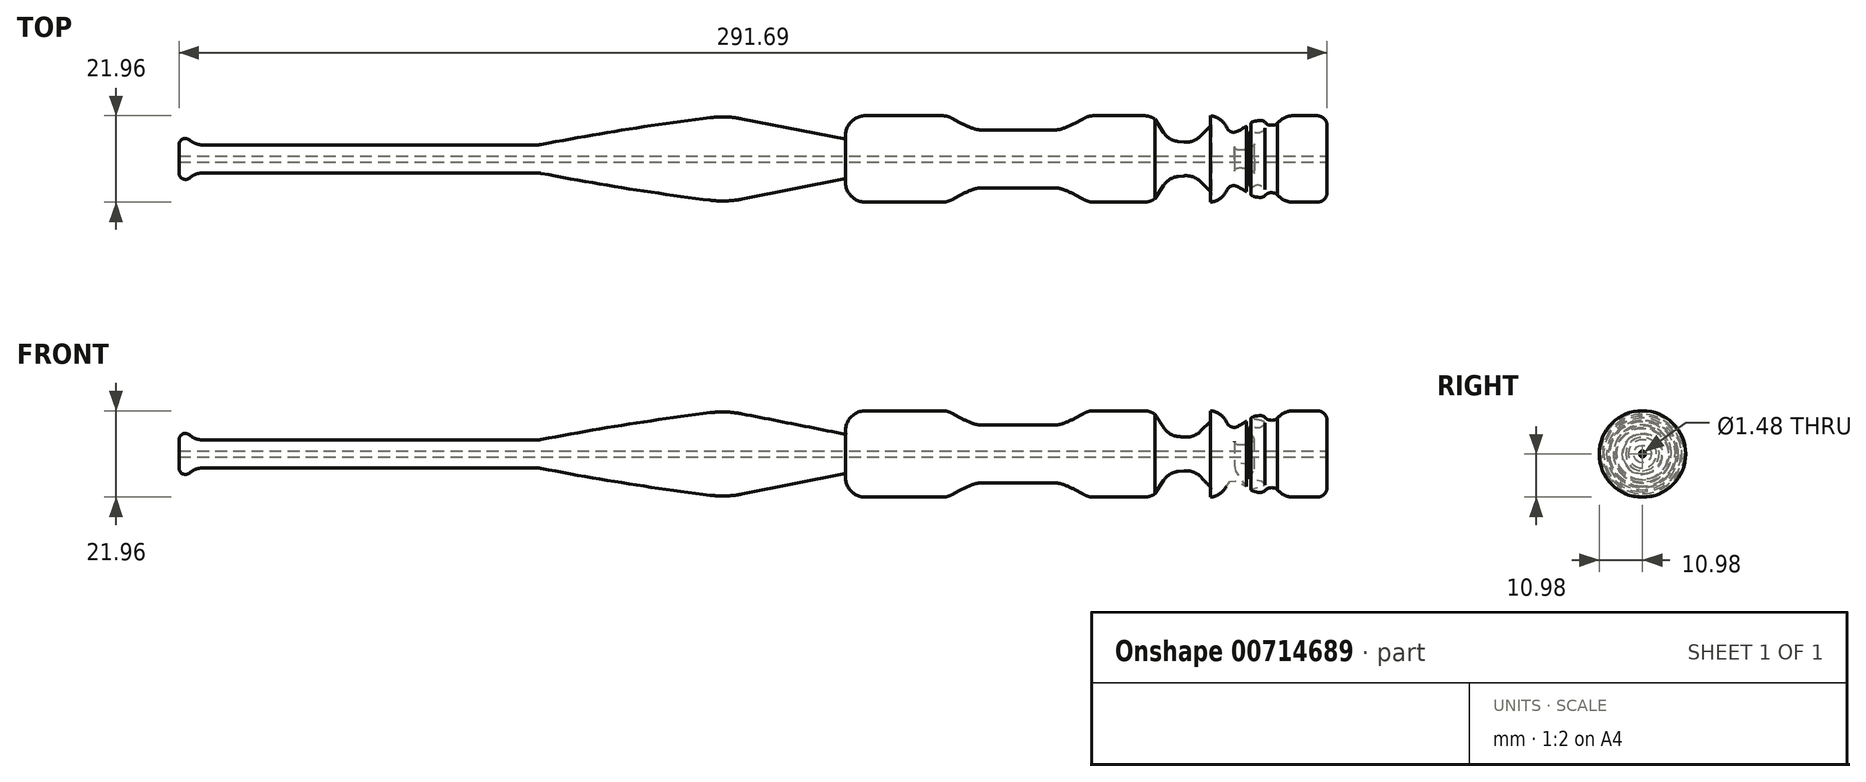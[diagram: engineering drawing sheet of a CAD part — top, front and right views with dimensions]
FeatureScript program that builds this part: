
annotation { "Feature Type Name" : "Feature", "Feature Type Description" : "" }
export const myFeature = defineFeature(function(context is Context, id is Id, definition is map)
    precondition{}
    {
        {
            var Q0;
            Q0=qCreatedBy(makeId("Front.planeOp"),FACE);
            var sketch = newSketch(context, id + "F0", { "sketchPlane" : qUnion([Q0])});
            skLineSegment(sketch, "E0", {"start": v(130.82, 0) * mm, "end": v(-159.34, 0) * mm});
            skPoint(sketch, "E1", {"position": v(-67.83, 3.57) * mm});
            skLineSegment(sketch, "E2", {"start": v(-67.83, 3.57) * mm, "end": v(-156.08, 3.57) * mm});
            skLineSegment(sketch, "E3", {"start": v(-159.34, 3.57) * mm, "end": v(-159.34, 0) * mm});
            skArc(sketch, "E4", {"start": v(132.48, 10.3) * mm, "mid": v(132.41, 10.3) * mm, "end": v(132.35, 10.3) * mm});
            skLineSegment(sketch, "E5", {"start": v(7.87, 10.98) * mm, "end": v(36.01, 10.98) * mm});
            skArc(sketch, "E6.trimOffspring", {"start": v(-20.28, 10.98) * mm, "mid": v(-44.13, 7.73) * mm, "end": v(-67.83, 3.57) * mm});
            skArc(sketch, "E7", {"start": v(-156.08, 3.57) * mm, "mid": v(-157.7, 5.2) * mm, "end": v(-159.34, 3.57) * mm});
            skLineSegment(sketch, "E8", {"start": v(126.85, 10.98) * mm, "end": v(129.81, 10.98) * mm});
            skLineSegment(sketch, "E9", {"start": v(132.35, 8.44) * mm, "end": v(132.35, 0) * mm});
            skLineSegment(sketch, "E10", {"start": v(132.35, 0) * mm, "end": v(130.82, 0) * mm});
            skPoint(sketch, "E11.visualSharp", {"position": v(132.35, 10.98) * mm});
            skArc(sketch, "E11.filletArc", {"start": v(132.35, 8.44) * mm, "mid": v(131.6, 10.23) * mm, "end": v(129.81, 10.98) * mm});
            skArc(sketch, "E12", {"start": v(36.01, 10.98) * mm, "mid": v(39.59, 8.95) * mm, "end": v(43.39, 7.4) * mm});
            skLineSegment(sketch, "E13.trimOffspring", {"start": v(71.63, 10.98) * mm, "end": v(88.94, 10.98) * mm});
            skLineSegment(sketch, "E14.bottom", {"start": v(43.39, 7.4) * mm, "end": v(64.25, 7.4) * mm});
            skArc(sketch, "E15.trimOffspring", {"start": v(64.25, 7.4) * mm, "mid": v(68.05, 8.95) * mm, "end": v(71.63, 10.98) * mm});
            skLineSegment(sketch, "E16.0", {"start": v(102.94, 8.6) * mm, "end": v(98.46, 4.04) * mm});
            skLineSegment(sketch, "E16.1", {"start": v(98.46, 4.04) * mm, "end": v(92.1, 4.7) * mm});
            skLineSegment(sketch, "E16.2", {"start": v(92.1, 4.7) * mm, "end": v(88.63, 10.08) * mm});
            skLineSegment(sketch, "E16.3", {"start": v(88.63, 10.08) * mm, "end": v(88.94, 10.98) * mm});
            skLineSegment(sketch, "E16.6", {"start": v(102.65, 10.98) * mm, "end": v(102.94, 8.6) * mm});
            skPoint(sketch, "E16.0.midPoint", {"position": v(100.7, 6.32) * mm});
            skLineSegment(sketch, "E17.trimOffspring", {"start": v(102.6, 10.98) * mm, "end": v(105.77, 10.98) * mm});
            skLineSegment(sketch, "E18", {"start": v(-20.28, 10.98) * mm, "end": v(10.06, 4.99) * mm});
            skLineSegment(sketch, "E19", {"start": v(10.06, 4.99) * mm, "end": v(7.87, 10.98) * mm});
            skFitSpline(sketch, "E20", {"points": [v(105.77, 10.98) * mm, v(108.63, 6.75) * mm, v(111.8, 8.24) * mm, v(108.88, 2.8) * mm, v(113.69, 3.37) * mm, v(112.91, 5.52) * mm, v(113.1, 7.27) * mm, v(114.47, 6.56) * mm, v(116.48, 7.73) * mm, v(115.31, 8.57) * mm, v(112.98, 9.09) * mm, v(115.77, 9.74) * mm, v(117.26, 8.76) * mm, v(119.6, 8.96) * mm, v(120.18, 10.98) * mm], "startDerivative": vector(20.04, -66.86) * mm, "endDerivative": vector(1.24, 38.02) * mm});
            skLineSegment(sketch, "E21.trimOffspring", {"start": v(120.18, 10.98) * mm, "end": v(126.85, 10.98) * mm});
            skSolve(sketch);
        }
        {
            var Q0;
            Q0=makeQuery(id+"F0.imprint","IMPRINT",FACE,{"disambiguationData":[TD([[makeQuery(id+"F0.imprint","IMPRINT",EDGE,{"derivedFrom":sQuery(id+"F0.wireOp",EDGE,"E0")}),-1.0]])]});
            var Q1;
            Q1=sQuery(id+"F0.wireOp",EDGE,"E0");
            revolve(context, id + "F1", {"surfaceOperationType" : NewSurfaceOperationType.NEW, "entities" : qUnion([Q0]), "axis" : qUnion([Q1]), "revolveType" : RevolveType.FULL});
        }
        {
            var Q0;
            Q0=makeQuery(id+"F1.opRevolve","SWEPT_FACE",FACE,{"disambiguationData":[OSD([sQuery(id+"F0.wireOp",EDGE,"E9")])]});
            var sketch = newSketch(context, id + "F2", { "sketchPlane" : qUnion([Q0])});
            skCircle(sketch, "E22", {"center": v(0, 0) * mm, "radius": 0.74 * mm});
            skSolve(sketch);
        }
        {
            var Q0;
            Q0=makeQuery(id+"F2.imprint","IMPRINT",FACE,{"disambiguationData":[TD([[makeQuery(id+"F2.imprint","IMPRINT",EDGE,{"derivedFrom":sQuery(id+"F2.wireOp",EDGE,"E22")}),1.0]])]});
            extrude(context, id + "F3", {"entities" : qUnion([Q0]), "operationType" : NewBodyOperationType.REMOVE, "endBound" : BoundingType.THROUGH_ALL, "oppositeDirection" : true, "depth" : 25.4 * mm, "offsetDistance" : 25.4 * mm});
        }
        {
            var Q0;
            Q0=makeQuery(id+"F1.opRevolve","SWEPT_EDGE",EDGE,{"disambiguationData":[OSD([sQuery(id+"F0.wireOp",EDGE,"E6.trimOffspring"),sQuery(id+"F0.wireOp",EDGE,"E18")])]});
            fillet(context, id + "F4", {"entities" : qUnion([Q0]), "radius" : 25.4 * mm, "tangentPropagation" : true, "allowEdgeOverflow" : false});
        }
        {
            var Q0;
            Q0=makeQuery(id+"F1.opRevolve","SWEPT_EDGE",EDGE,{"disambiguationData":[OSD([sQuery(id+"F0.wireOp",EDGE,"E2"),sQuery(id+"F0.wireOp",EDGE,"E6.trimOffspring")])]});
            var Q1;
            Q1=makeQuery(id+"F1.opRevolve","SWEPT_FACE",FACE,{"disambiguationData":[OSD([sQuery(id+"F0.wireOp",EDGE,"E7")])]});
            var Q2;
            Q2=makeQuery(id+"F1.opRevolve","SWEPT_EDGE",EDGE,{"disambiguationData":[OSD([sQuery(id+"F0.wireOp",EDGE,"E12"),sQuery(id+"F0.wireOp",EDGE,"E14.bottom")])]});
            var Q3;
            Q3=makeQuery(id+"F1.opRevolve","SWEPT_EDGE",EDGE,{"disambiguationData":[OSD([sQuery(id+"F0.wireOp",EDGE,"E14.bottom"),sQuery(id+"F0.wireOp",EDGE,"E15.trimOffspring")])]});
            var Q4;
            Q4=makeQuery(id+"F1.opRevolve","SWEPT_EDGE",EDGE,{"disambiguationData":[OSD([sQuery(id+"F0.wireOp",EDGE,"E13.trimOffspring"),sQuery(id+"F0.wireOp",EDGE,"E15.trimOffspring")])]});
            var Q5;
            Q5=makeQuery(id+"F1.opRevolve","SWEPT_EDGE",EDGE,{"disambiguationData":[OSD([sQuery(id+"F0.wireOp",EDGE,"E5"),sQuery(id+"F0.wireOp",EDGE,"E12")])]});
            var Q6;
            Q6=makeQuery(id+"F1.opRevolve","SWEPT_EDGE",EDGE,{"disambiguationData":[OSD([sQuery(id+"F0.wireOp",EDGE,"E5"),sQuery(id+"F0.wireOp",EDGE,"E19")])]});
            var Q7;
            Q7=makeQuery(id+"F1.opRevolve","SWEPT_FACE",FACE,{"disambiguationData":[OSD([sQuery(id+"F0.wireOp",EDGE,"E16.1")])]});
            var Q8;
            Q8=makeQuery(id+"F1.opRevolve","SWEPT_FACE",FACE,{"disambiguationData":[OSD([sQuery(id+"F0.wireOp",EDGE,"E13.trimOffspring")])]});
            var Q9;
            Q9=makeQuery(id+"F1.opRevolve","SWEPT_FACE",FACE,{"disambiguationData":[OSD([sQuery(id+"F0.wireOp",EDGE,"E20")])]});
            var Q10;
            Q10=makeQuery(id+"F1.opRevolve","SWEPT_FACE",FACE,{"disambiguationData":[OSD([sQuery(id+"F0.wireOp",EDGE,"E11.filletArc")])]});
            var Q11;
            Q11=makeQuery(id+"F1.opRevolve","SWEPT_FACE",FACE,{"disambiguationData":[OSD([sQuery(id+"F0.wireOp",EDGE,"E8"),sQuery(id+"F0.wireOp",EDGE,"E21.trimOffspring")])]});
            fillet(context, id + "F5", {"entities" : qUnion([Q0, Q1, Q2, Q3, Q4, Q5, Q6, Q7, Q8, Q9, Q10, Q11]), "radius" : 5.08 * mm, "tangentPropagation" : true, "allowEdgeOverflow" : false});
        }
    });
